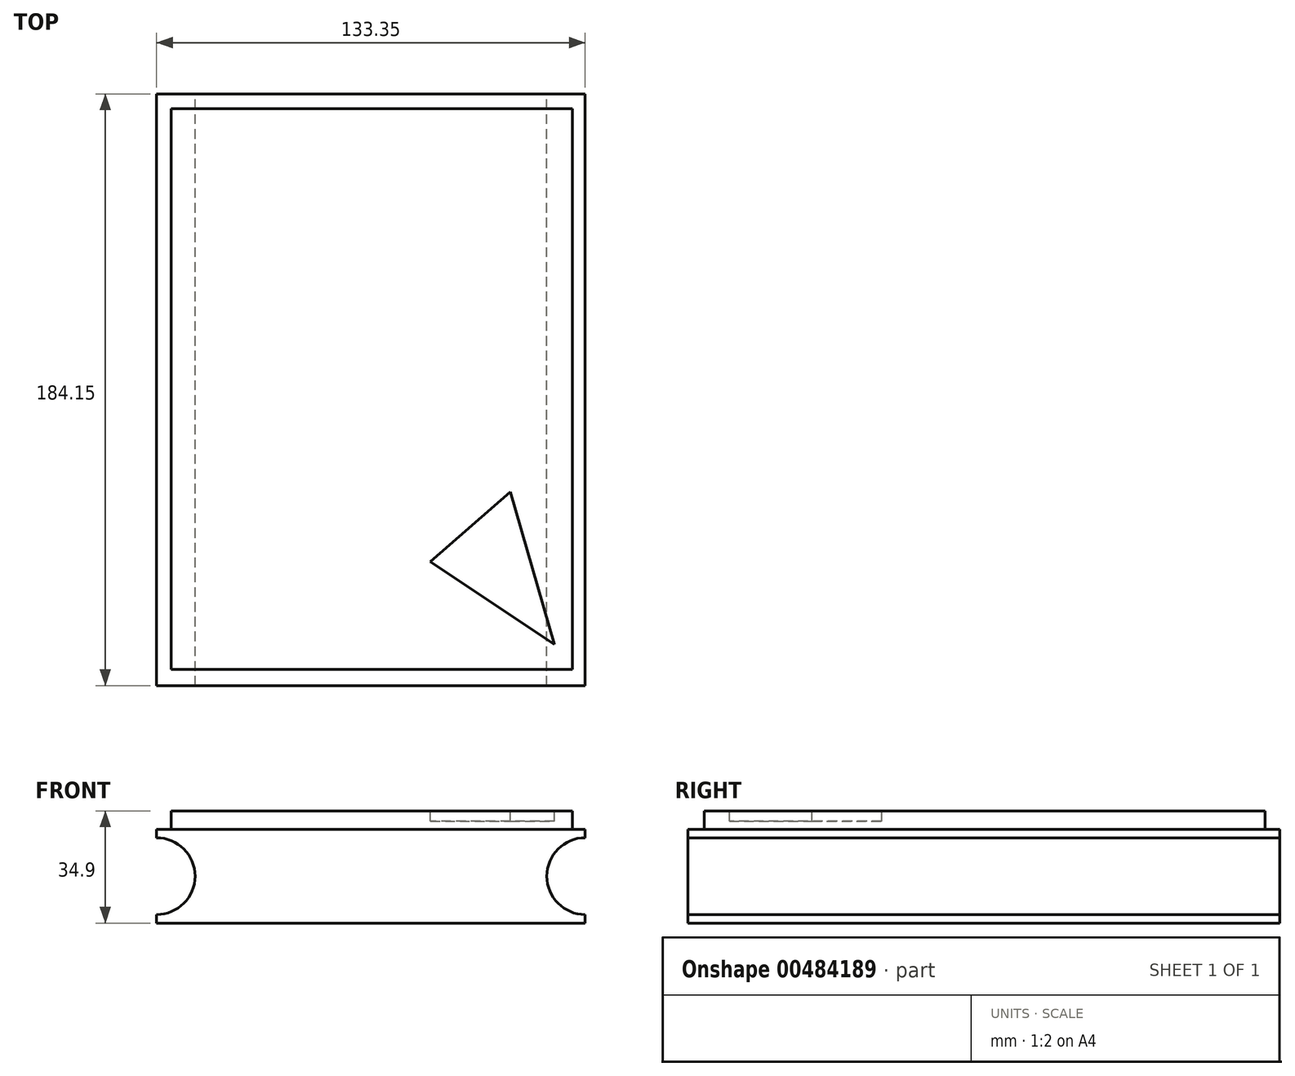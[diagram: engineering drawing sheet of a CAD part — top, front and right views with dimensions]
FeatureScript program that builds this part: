
annotation { "Feature Type Name" : "Feature", "Feature Type Description" : "" }
export const myFeature = defineFeature(function(context is Context, id is Id, definition is map)
    precondition{}
    {
        {
            var Q0;
            Q0=qCreatedBy(makeId("Front.planeOp"),FACE);
            var sketch = newSketch(context, id + "F0", { "sketchPlane" : qUnion([Q0])});
            skLineSegment(sketch, "E0.bottom", {"start": v(0, 0) * mm, "end": v(133.35, 0) * mm});
            skLineSegment(sketch, "E0.top", {"start": v(0, 29.19) * mm, "end": v(133.35, 29.19) * mm});
            skLineSegment(sketch, "E0.left", {"start": v(0, 0) * mm, "end": v(0, 29.19) * mm, "construction": true});
            skLineSegment(sketch, "E0.right", {"start": v(133.35, 0) * mm, "end": v(133.35, 29.19) * mm, "construction": true});
            skArc(sketch, "E1", {"start": v(0, 2.64) * mm, "mid": v(11.95, 14.6) * mm, "end": v(0, 26.55) * mm});
            skArc(sketch, "E2", {"start": v(133.35, 26.55) * mm, "mid": v(121.4, 14.6) * mm, "end": v(133.35, 2.64) * mm});
            skLineSegment(sketch, "E3", {"start": v(0, 29.19) * mm, "end": v(0, 26.55) * mm});
            skLineSegment(sketch, "E4", {"start": v(0, 2.64) * mm, "end": v(0, 0) * mm});
            skLineSegment(sketch, "E5", {"start": v(133.35, 29.19) * mm, "end": v(133.35, 26.55) * mm});
            skLineSegment(sketch, "E6", {"start": v(133.35, 2.64) * mm, "end": v(133.35, 0) * mm});
            skSolve(sketch);
        }
        {
            var Q0;
            Q0 = qSketchRegion(id + "F0", true);
            extrude(context, id + "F1", {"entities" : qUnion([Q0]), "depth" : 184.15 * mm});
        }
        {
            var Q0;
            Q0=makeQuery(id+"F1.opExtrude","SWEPT_FACE",FACE,{"disambiguationData":[OSD([sQuery(id+"F0.wireOp",EDGE,"E0.top")])]});
            var sketch = newSketch(context, id + "F2", { "sketchPlane" : qUnion([Q0])});
            skLineSegment(sketch, "E7.bottom", {"start": v(4.57, -179.15) * mm, "end": v(129.36, -179.15) * mm});
            skLineSegment(sketch, "E7.top", {"start": v(4.57, -4.57) * mm, "end": v(129.36, -4.57) * mm});
            skLineSegment(sketch, "E7.left", {"start": v(4.57, -179.15) * mm, "end": v(4.57, -4.57) * mm});
            skLineSegment(sketch, "E7.right", {"start": v(129.36, -179.15) * mm, "end": v(129.36, -4.57) * mm});
            skSolve(sketch);
        }
        {
            var Q0;
            Q0 = qSketchRegion(id + "F2", true);
            extrude(context, id + "F3", {"entities" : qUnion([Q0]), "operationType" : NewBodyOperationType.ADD, "depth" : 5.7 * mm});
        }
        {
            var Q0;
            Q0=makeQuery(id+"F3.opExtrude","CAP_FACE",FACE,{"disambiguationData":[OSD([sQuery(id+"F2.wireOp",EDGE,"E7.bottom"),sQuery(id+"F2.wireOp",EDGE,"E7.top"),sQuery(id+"F2.wireOp",EDGE,"E7.left"),sQuery(id+"F2.wireOp",EDGE,"E7.right")])],"isStart":false});
            var sketch = newSketch(context, id + "F4", { "sketchPlane" : qUnion([Q0])});
            skLineSegment(sketch, "E8", {"start": v(123.75, -171.3) * mm, "end": v(85.2, -145.58) * mm});
            skLineSegment(sketch, "E9", {"start": v(85.2, -145.58) * mm, "end": v(110.02, -123.88) * mm});
            skLineSegment(sketch, "E10", {"start": v(110.02, -123.88) * mm, "end": v(123.75, -171.3) * mm});
            skLineSegment(sketch, "E11", {"start": v(129.36, -179.15) * mm, "end": v(4.57, -4.57) * mm, "construction": true});
            skPoint(sketch, "E12", {"position": v(97.61, -134.73) * mm});
            skSolve(sketch);
        }
        {
            var Q0;
            Q0=makeQuery(id+"F4.imprint","IMPRINT",FACE,{"disambiguationData":[TD([[makeQuery(id+"F4.imprint","IMPRINT",EDGE,{"derivedFrom":sQuery(id+"F4.wireOp",EDGE,"E8")}),-1.0]])]});
            extrude(context, id + "F5", {"entities" : qUnion([Q0]), "operationType" : NewBodyOperationType.REMOVE, "oppositeDirection" : true, "depth" : 3.17 * mm});
        }
    });
